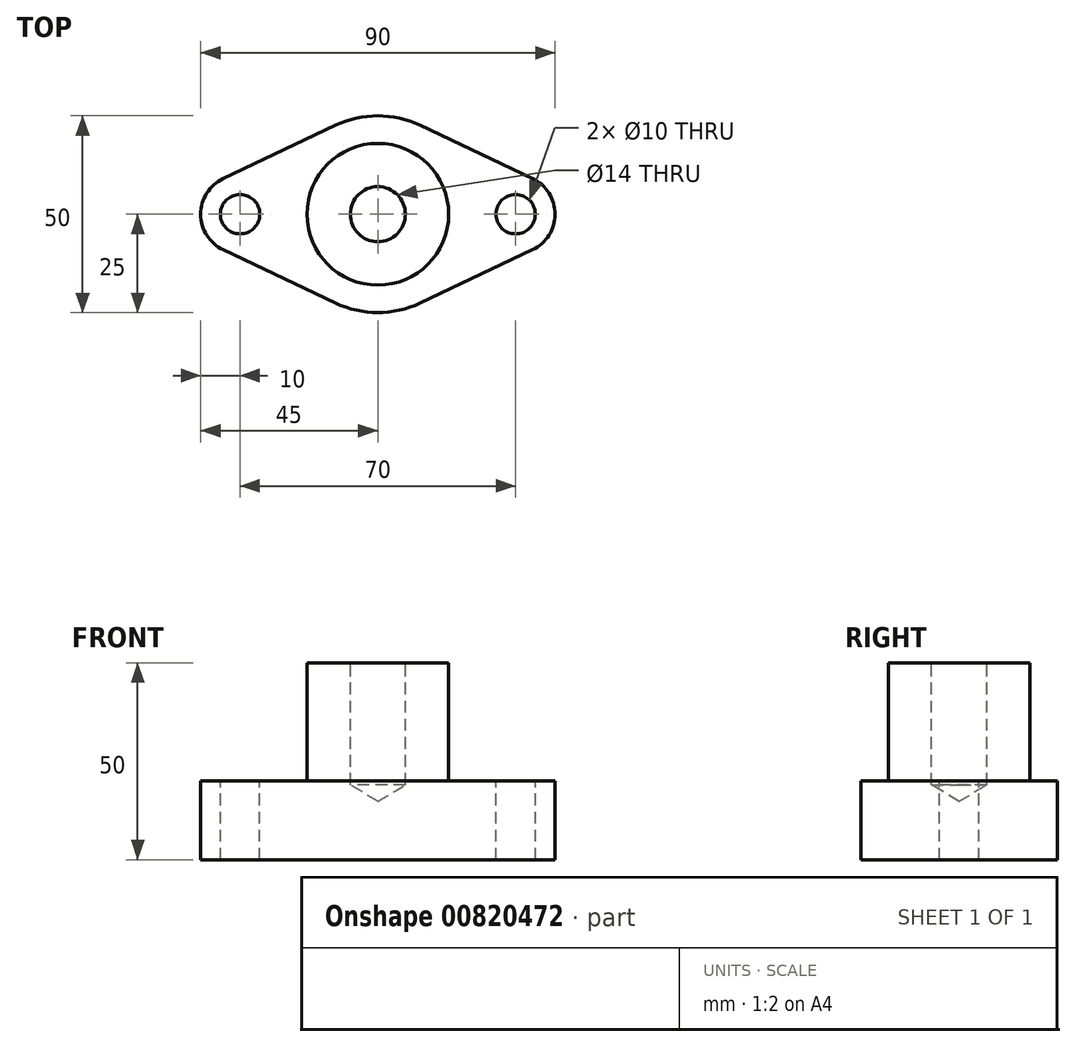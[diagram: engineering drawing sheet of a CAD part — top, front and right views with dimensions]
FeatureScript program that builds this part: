
annotation { "Feature Type Name" : "Feature", "Feature Type Description" : "" }
export const myFeature = defineFeature(function(context is Context, id is Id, definition is map)
    precondition{}
    {
        {
            var Q0;
            Q0=qCreatedBy(makeId("Top.planeOp"),FACE);
            var sketch = newSketch(context, id + "F0", { "sketchPlane" : qUnion([Q0])});
            skCircle(sketch, "E0", {"center": v(0, 0) * mm, "radius": 25 * mm});
            skLineSegment(sketch, "E1", {"start": v(0, 0) * mm, "end": v(35, 0) * mm});
            skLineSegment(sketch, "E2", {"start": v(0, 0) * mm, "end": v(-35, 0) * mm});
            skCircle(sketch, "E3", {"center": v(-35, 0) * mm, "radius": 10 * mm});
            skCircle(sketch, "E4", {"center": v(35, 0) * mm, "radius": 10 * mm});
            skCircle(sketch, "E5", {"center": v(0, 0) * mm, "radius": 18 * mm});
            skLineSegment(sketch, "E6", {"start": v(39.29, 9.04) * mm, "end": v(10.71, 22.59) * mm});
            skLineSegment(sketch, "E7", {"start": v(39.29, -9.04) * mm, "end": v(10.71, -22.59) * mm});
            skLineSegment(sketch, "E8", {"start": v(-39.29, 9.04) * mm, "end": v(-10.71, 22.59) * mm});
            skLineSegment(sketch, "E9", {"start": v(-39.29, -9.04) * mm, "end": v(-10.71, -22.59) * mm});
            skSolve(sketch);
        }
        {
            var Q0;
            {var subQ0=sQuery(id+"F0.wireOp",EDGE,"E9");var subQ1=sQuery(id+"F0.wireOp",EDGE,"E0");var subQ2=makeQuery(id+"F0.imprint","INTERSECT",VERTEX,{"derivedFrom":[subQ1,subQ0]});Q0=makeQuery(id+"F0.imprint","IMPRINT",FACE,{"disambiguationData":[TD([[makeQuery(id+"F0.imprint","IMPRINT",EDGE,{"disambiguationData":[TD([[subQ2,1.0]])],"derivedFrom":subQ0}),1.0]])]});}
            var Q1;
            {var subQ0=sQuery(id+"F0.wireOp",EDGE,"E8");var subQ1=sQuery(id+"F0.wireOp",EDGE,"E3");var subQ2=makeQuery(id+"F0.imprint","INTERSECT",VERTEX,{"disambiguationData":[OD(0.0)],"derivedFrom":[subQ1,subQ0]});Q1=makeQuery(id+"F0.imprint","IMPRINT",FACE,{"disambiguationData":[TD([[makeQuery(id+"F0.imprint","IMPRINT",EDGE,{"disambiguationData":[TD([[subQ2,1.0]])],"derivedFrom":subQ1}),1.0]])]});}
            var Q2;
            {var subQ0=sQuery(id+"F0.wireOp",EDGE,"E2");var subQ1=sQuery(id+"F0.wireOp",EDGE,"E1");var subQ2=makeQuery(id+"F0.imprint","INTERSECT",VERTEX,{"derivedFrom":[subQ1,subQ0]});Q2=makeQuery(id+"F0.imprint","IMPRINT",FACE,{"disambiguationData":[TD([[makeQuery(id+"F0.imprint","IMPRINT",EDGE,{"disambiguationData":[TD([[subQ2,-1.0]])],"derivedFrom":subQ1}),1.0]])]});}
            var Q3;
            {var subQ0=sQuery(id+"F0.wireOp",EDGE,"E2");var subQ1=sQuery(id+"F0.wireOp",EDGE,"E1");var subQ2=makeQuery(id+"F0.imprint","INTERSECT",VERTEX,{"derivedFrom":[subQ1,subQ0]});Q3=makeQuery(id+"F0.imprint","IMPRINT",FACE,{"disambiguationData":[TD([[makeQuery(id+"F0.imprint","IMPRINT",EDGE,{"disambiguationData":[TD([[subQ2,-1.0]])],"derivedFrom":subQ1}),-1.0]])]});}
            var Q4;
            {var subQ3=sQuery(id+"F0.wireOp",EDGE,"E0");var subQ5=makeQuery(id+"F0.imprint","INTERSECT",VERTEX,{"derivedFrom":[subQ3,sQuery(id+"F0.wireOp",EDGE,"E7")]});Q4=makeQuery(id+"F0.imprint","IMPRINT",FACE,{"disambiguationData":[TD([[makeQuery(id+"F0.imprint","IMPRINT",EDGE,{"disambiguationData":[TD([[subQ5,1.0]])],"derivedFrom":subQ3}),1.0]])]});}
            var Q5;
            {var subQ0=sQuery(id+"F0.wireOp",EDGE,"E9");var subQ1=sQuery(id+"F0.wireOp",EDGE,"E3");var subQ2=makeQuery(id+"F0.imprint","INTERSECT",VERTEX,{"disambiguationData":[OD(0.0)],"derivedFrom":[subQ1,subQ0]});Q5=makeQuery(id+"F0.imprint","IMPRINT",FACE,{"disambiguationData":[TD([[makeQuery(id+"F0.imprint","IMPRINT",EDGE,{"disambiguationData":[TD([[subQ2,-1.0]])],"derivedFrom":subQ1}),1.0]])]});}
            var Q6;
            {var subQ0=sQuery(id+"F0.wireOp",EDGE,"E7");var subQ1=sQuery(id+"F0.wireOp",EDGE,"E0");var subQ2=makeQuery(id+"F0.imprint","INTERSECT",VERTEX,{"derivedFrom":[subQ1,subQ0]});Q6=makeQuery(id+"F0.imprint","IMPRINT",FACE,{"disambiguationData":[TD([[makeQuery(id+"F0.imprint","IMPRINT",EDGE,{"disambiguationData":[TD([[subQ2,1.0]])],"derivedFrom":subQ0}),-1.0]])]});}
            var Q7;
            {var subQ0=sQuery(id+"F0.wireOp",EDGE,"E6");var subQ1=sQuery(id+"F0.wireOp",EDGE,"E4");var subQ2=makeQuery(id+"F0.imprint","INTERSECT",VERTEX,{"disambiguationData":[OD(0.0)],"derivedFrom":[subQ1,subQ0]});Q7=makeQuery(id+"F0.imprint","IMPRINT",FACE,{"disambiguationData":[TD([[makeQuery(id+"F0.imprint","IMPRINT",EDGE,{"disambiguationData":[TD([[subQ2,1.0]])],"derivedFrom":subQ1}),1.0]])]});}
            var Q8;
            {var subQ0=sQuery(id+"F0.wireOp",EDGE,"E8");var subQ1=sQuery(id+"F0.wireOp",EDGE,"E3");var subQ2=makeQuery(id+"F0.imprint","INTERSECT",VERTEX,{"disambiguationData":[OD(0.0)],"derivedFrom":[subQ1,subQ0]});Q8=makeQuery(id+"F0.imprint","IMPRINT",FACE,{"disambiguationData":[TD([[makeQuery(id+"F0.imprint","IMPRINT",EDGE,{"disambiguationData":[TD([[subQ2,-1.0]])],"derivedFrom":subQ1}),1.0]])]});}
            var Q9;
            {var subQ0=sQuery(id+"F0.wireOp",EDGE,"E6");var subQ1=sQuery(id+"F0.wireOp",EDGE,"E0");var subQ2=makeQuery(id+"F0.imprint","INTERSECT",VERTEX,{"derivedFrom":[subQ1,subQ0]});Q9=makeQuery(id+"F0.imprint","IMPRINT",FACE,{"disambiguationData":[TD([[makeQuery(id+"F0.imprint","IMPRINT",EDGE,{"disambiguationData":[TD([[subQ2,1.0]])],"derivedFrom":subQ0}),1.0]])]});}
            var Q10;
            {var subQ0=sQuery(id+"F0.wireOp",EDGE,"E8");var subQ1=sQuery(id+"F0.wireOp",EDGE,"E0");var subQ2=makeQuery(id+"F0.imprint","INTERSECT",VERTEX,{"derivedFrom":[subQ1,subQ0]});Q10=makeQuery(id+"F0.imprint","IMPRINT",FACE,{"disambiguationData":[TD([[makeQuery(id+"F0.imprint","IMPRINT",EDGE,{"disambiguationData":[TD([[subQ2,1.0]])],"derivedFrom":subQ0}),-1.0]])]});}
            var Q11;
            {var subQ0=sQuery(id+"F0.wireOp",EDGE,"E6");var subQ1=sQuery(id+"F0.wireOp",EDGE,"E4");var subQ2=makeQuery(id+"F0.imprint","INTERSECT",VERTEX,{"disambiguationData":[OD(0.0)],"derivedFrom":[subQ1,subQ0]});Q11=makeQuery(id+"F0.imprint","IMPRINT",FACE,{"disambiguationData":[TD([[makeQuery(id+"F0.imprint","IMPRINT",EDGE,{"disambiguationData":[TD([[subQ2,-1.0]])],"derivedFrom":subQ1}),1.0]])]});}
            var Q12;
            {var subQ0=sQuery(id+"F0.wireOp",EDGE,"E7");var subQ1=sQuery(id+"F0.wireOp",EDGE,"E4");var subQ2=makeQuery(id+"F0.imprint","INTERSECT",VERTEX,{"disambiguationData":[OD(0.0)],"derivedFrom":[subQ1,subQ0]});Q12=makeQuery(id+"F0.imprint","IMPRINT",FACE,{"disambiguationData":[TD([[makeQuery(id+"F0.imprint","IMPRINT",EDGE,{"disambiguationData":[TD([[subQ2,1.0]])],"derivedFrom":subQ1}),1.0]])]});}
            var Q13;
            {var subQ3=sQuery(id+"F0.wireOp",EDGE,"E0");var subQ8=makeQuery(id+"F0.imprint","INTERSECT",VERTEX,{"derivedFrom":[subQ3,sQuery(id+"F0.wireOp",EDGE,"E6")]});Q13=makeQuery(id+"F0.imprint","IMPRINT",FACE,{"disambiguationData":[TD([[makeQuery(id+"F0.imprint","IMPRINT",EDGE,{"disambiguationData":[TD([[subQ8,-1.0]])],"derivedFrom":subQ3}),1.0]])]});}
            extrude(context, id + "F1", {"entities" : qUnion([Q0, Q1, Q2, Q3, Q4, Q5, Q6, Q7, Q8, Q9, Q10, Q11, Q12, Q13]), "oppositeDirection" : true, "depth" : 20 * mm, "offsetDistance" : 25 * mm});
        }
        {
            var Q0;
            {var subQ0=sQuery(id+"F0.wireOp",EDGE,"E2");var subQ1=sQuery(id+"F0.wireOp",EDGE,"E1");var subQ2=makeQuery(id+"F0.imprint","INTERSECT",VERTEX,{"derivedFrom":[subQ1,subQ0]});Q0=makeQuery(id+"F0.imprint","IMPRINT",FACE,{"disambiguationData":[TD([[makeQuery(id+"F0.imprint","IMPRINT",EDGE,{"disambiguationData":[TD([[subQ2,-1.0]])],"derivedFrom":subQ1}),1.0]])]});}
            var Q1;
            {var subQ0=sQuery(id+"F0.wireOp",EDGE,"E2");var subQ1=sQuery(id+"F0.wireOp",EDGE,"E1");var subQ2=makeQuery(id+"F0.imprint","INTERSECT",VERTEX,{"derivedFrom":[subQ1,subQ0]});Q1=makeQuery(id+"F0.imprint","IMPRINT",FACE,{"disambiguationData":[TD([[makeQuery(id+"F0.imprint","IMPRINT",EDGE,{"disambiguationData":[TD([[subQ2,-1.0]])],"derivedFrom":subQ1}),-1.0]])]});}
            extrude(context, id + "F2", {"entities" : qUnion([Q0, Q1]), "operationType" : NewBodyOperationType.ADD, "depth" : 30 * mm, "offsetDistance" : 25 * mm});
        }
        {
            var Q0;
            Q0=sQuery(id+"F0.wireOp",VERTEX,"E2.end");
            var Q1;
            Q1=sQuery(id+"F0.wireOp",VERTEX,"E1.end");
            var Q2;
            Q2=makeQuery(id+"F1.opExtrude","SWEPT_BODY",BODY,{"disambiguationData":[OSD([sQuery(id+"F0.wireOp",EDGE,"E0"),sQuery(id+"F0.wireOp",EDGE,"E3"),sQuery(id+"F0.wireOp",EDGE,"E4"),sQuery(id+"F0.wireOp",EDGE,"E6"),sQuery(id+"F0.wireOp",EDGE,"E7"),sQuery(id+"F0.wireOp",EDGE,"E8"),sQuery(id+"F0.wireOp",EDGE,"E9")])]});
            hole(context, id + "F3", {"style" : HoleStyle.SIMPLE, "endStyle" : HoleEndStyle.THROUGH, "holeDiameter" : 10 * mm, "majorDiameter" : 5 * mm, "isTappedThrough" : true, "tappedDepth" : 12 * mm, "tapClearance" : 3, "startFromSketch" : true, "locations" : qUnion([Q0, Q1]), "scope" : qUnion([Q2])});
        }
        {
            var Q0;
            Q0=makeQuery(id+"F2.opExtrude","CAP_FACE",FACE,{"disambiguationData":[OSD([sQuery(id+"F0.wireOp",EDGE,"E5")])],"isStart":false});
            var sketch = newSketch(context, id + "F4", { "sketchPlane" : qUnion([Q0])});
            skLineSegment(sketch, "E10", {"start": v(0, 18) * mm, "end": v(0, 0) * mm});
            skSolve(sketch);
        }
        {
            var Q0;
            Q0=sQuery(id+"F4.wireOp",VERTEX,"E10.end");
            var Q1;
            Q1=makeQuery(id+"F1.opExtrude","SWEPT_BODY",BODY,{"disambiguationData":[OSD([sQuery(id+"F0.wireOp",EDGE,"E0"),sQuery(id+"F0.wireOp",EDGE,"E3"),sQuery(id+"F0.wireOp",EDGE,"E4"),sQuery(id+"F0.wireOp",EDGE,"E6"),sQuery(id+"F0.wireOp",EDGE,"E7"),sQuery(id+"F0.wireOp",EDGE,"E8"),sQuery(id+"F0.wireOp",EDGE,"E9")])]});
            hole(context, id + "F5", {"style" : HoleStyle.SIMPLE, "endStyle" : HoleEndStyle.BLIND, "standardTappedOrClearance" : lookupTablePath({ "standard" : "ISO", "engagement" : "75%", "pitch" : "2 mm", "size" : "M16", "type" : "Tapped" }), "standardBlindInLast" : lookupTablePath({ "standard" : "ISO", "engagement" : "75%", "pitch" : "2 mm", "size" : "M16", "type" : "Tapped" }), "holeDiameter" : 14 * mm, "majorDiameter" : 16 * mm, "showTappedDepth" : true, "holeDepth" : 31 * mm, "isTappedThrough" : true, "tappedDepth" : 25 * mm, "tapClearance" : 3, "startFromSketch" : true, "locations" : qUnion([Q0]), "scope" : qUnion([Q1])});
        }
    });
